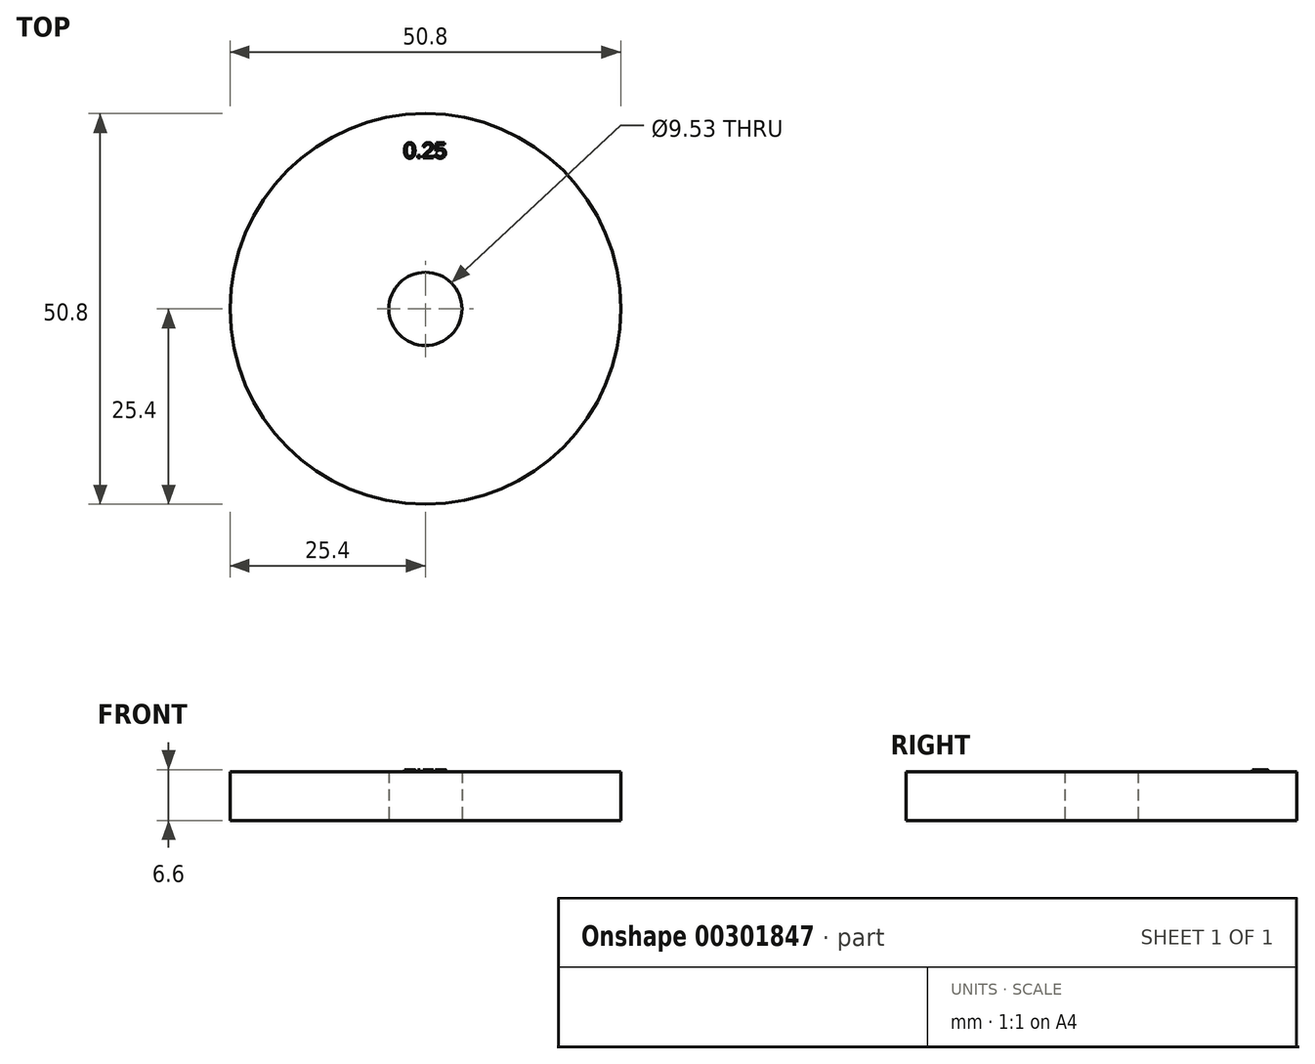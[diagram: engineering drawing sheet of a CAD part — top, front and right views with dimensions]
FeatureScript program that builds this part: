
annotation { "Feature Type Name" : "Feature", "Feature Type Description" : "" }
export const myFeature = defineFeature(function(context is Context, id is Id, definition is map)
    precondition{}
    {
        {
            var Q0;
            Q0=qCreatedBy(makeId("Top.planeOp"),FACE);
            var sketch = newSketch(context, id + "F0", { "sketchPlane" : qUnion([Q0])});
            skCircle(sketch, "E0", {"center": v(0, 0) * mm, "radius": 25.4 * mm});
            skCircle(sketch, "E1", {"center": v(0, 0) * mm, "radius": 4.76 * mm});
            skSolve(sketch);
        }
        {
            var Q0;
            Q0 = qSketchRegion(id + "F0", true);
            extrude(context, id + "F1", {"entities" : qUnion([Q0]), "depth" : 6.35 * mm});
        }
        {
            var Q0;
            Q0=makeQuery(id+"F1.opExtrude","CAP_FACE",FACE,{"disambiguationData":[OSD([sQuery(id+"F0.wireOp",EDGE,"E0"),sQuery(id+"F0.wireOp",EDGE,"E1")])],"isStart":false});
            var sketch = newSketch(context, id + "F2", { "sketchPlane" : qUnion([Q0])});
            skText(sketch, "E2", { "text": "0.25", "fontName": "Arimo-Regular.ttf"});
            const initialGuessF2  = {"E2": [-0.00283, 0.01962, 1, 0, 0.00206]};
            skSetInitialGuess(sketch, initialGuessF2);
            skSolve(sketch);
        }
        {
            var Q0;
            Q0 = qSketchRegion(id + "F2", true);
            extrude(context, id + "F3", {"entities" : qUnion([Q0]), "operationType" : NewBodyOperationType.ADD, "depth" : 0.25 * mm});
        }
    });
